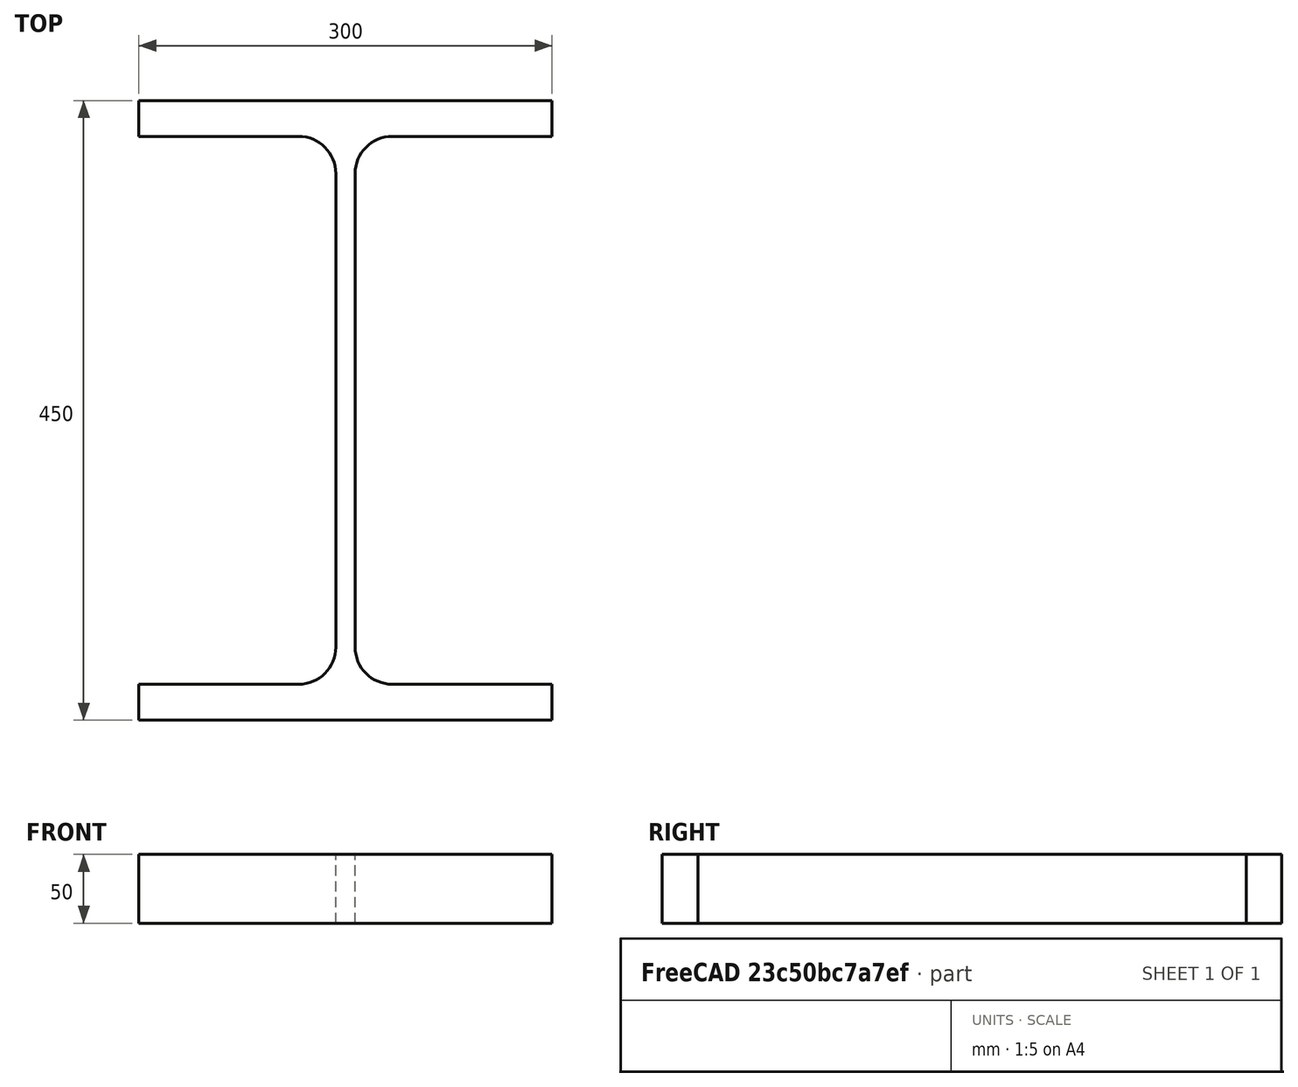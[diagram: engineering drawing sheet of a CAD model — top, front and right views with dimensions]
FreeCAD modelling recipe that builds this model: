
FCSTD DOCUMENT  (FreeCAD 0.15R4671 (Git))
Label: HE-B-Profile 450 DIN1025-2 S235JR
License: All rights reserved
LicenseURL: http://en.wikipedia.org/wiki/All_rights_reserved
objects: Sketcher::SketchObject×1, Part::Extrusion×1
note: 2 computed .brp shape members not serialized (recipe doc carries the construction recipe); baked Part::Feature solids carry a one-line shape summary decoded from their .brp

FEATURE [Sketcher::SketchObject] Sketch
  sketch-geometry (16):
    g0: LineSegment StartX=7 StartY=-172 StartZ=0 EndX=7 EndY=172 EndZ=0
    g1: LineSegment StartX=34 StartY=199 StartZ=0 EndX=150 EndY=199 EndZ=0
    g2: LineSegment StartX=150 StartY=199 StartZ=0 EndX=150 EndY=225 EndZ=0
    g3: LineSegment StartX=150 StartY=225 StartZ=0 EndX=-150 EndY=225 EndZ=0
    g4: LineSegment StartX=-150 StartY=225 StartZ=0 EndX=-150 EndY=199 EndZ=0
    g5: LineSegment StartX=-150 StartY=199 StartZ=0 EndX=-34 EndY=199 EndZ=0
    g6: LineSegment StartX=-7 StartY=172 StartZ=0 EndX=-7 EndY=-172 EndZ=0
    g7: LineSegment StartX=-34 StartY=-199 StartZ=0 EndX=-150 EndY=-199 EndZ=0
    g8: LineSegment StartX=-150 StartY=-199 StartZ=0 EndX=-150 EndY=-225 EndZ=0
    g9: LineSegment StartX=-150 StartY=-225 StartZ=0 EndX=150 EndY=-225 EndZ=0
    g10: LineSegment StartX=150 StartY=-225 StartZ=0 EndX=150 EndY=-199 EndZ=0
    g11: LineSegment StartX=150 StartY=-199 StartZ=0 EndX=34 EndY=-199 EndZ=0
    g12: ArcOfCircle CenterX=34 CenterY=172 CenterZ=0 NormalX=0 NormalY=0 NormalZ=1 Radius=27 StartAngle=1.5708 EndAngle=3.14159
    g13: ArcOfCircle CenterX=34 CenterY=-172 CenterZ=0 NormalX=0 NormalY=0 NormalZ=1 Radius=27 StartAngle=3.14159 EndAngle=4.71239
    g14: ArcOfCircle CenterX=-34 CenterY=172 CenterZ=0 NormalX=0 NormalY=0 NormalZ=1 Radius=27 StartAngle=0 EndAngle=1.5708
    g15: ArcOfCircle CenterX=-34 CenterY=-172 CenterZ=0 NormalX=0 NormalY=0 NormalZ=1 Radius=27 StartAngle=4.71239 EndAngle=6.28319
  constraints (42):
    c: Vertical(g0)
    c: Coincident(g2,g1)
    c: Vertical(g2)
    c: Coincident(g3,g2)
    c: Coincident(g4,g3)
    c: Vertical(g4)
    c: Coincident(g5,g4)
    c: Horizontal(g5)
    c: Vertical(g6)
    c: Horizontal(g7)
    c: Coincident(g8,g7)
    c: Vertical(g8)
    c: Coincident(g9,g8)
    c: Horizontal(g9)
    c: Coincident(g10,g9)
    c: Vertical(g10)
    c: Coincident(g11,g10)
    c: Horizontal(g11)
    c: Tangent(g1,g12) = 1.5708
    c: Tangent(g0,g12) = 1.5708
    c: Tangent(g0,g13) = 1.5708
    c: Tangent(g11,g13) = 1.5708
    c: Tangent(g5,g14) = 1.5708
    c: Tangent(g6,g14) = 1.5708
    c: Tangent(g6,g15) = 1.5708
    c: Tangent(g7,g15) = 1.5708
    c: Equal(g3,g9)
    c: Equal(g2,g4)
    c: Equal(g4,g8)
    c: Equal(g8,g10)
    c: Equal(g12,g14)
    c: Equal(g14,g15)
    c: Equal(g15,g13)
    c: Symmetric(g2,g3,g-2)
    c: Symmetric(g9,g8,g-2)
    c: Symmetric(g0,g6,g-2)
    c: Symmetric(g2,g9,g-1)
    c: DistanceY(g2,g9) = -450
    c: DistanceX(g3) = -300
    c: DistanceX(g0,g6) = -14
    c: DistanceY(g2) = 26
    c: Radius(g12) = 27
FEATURE [Part::Extrusion] Extrude  label="HE-B-Profile 450 DIN1025-2 S235JR"
  Base = -> Sketch
  Dir = (0,0,50)
  Solid = true
